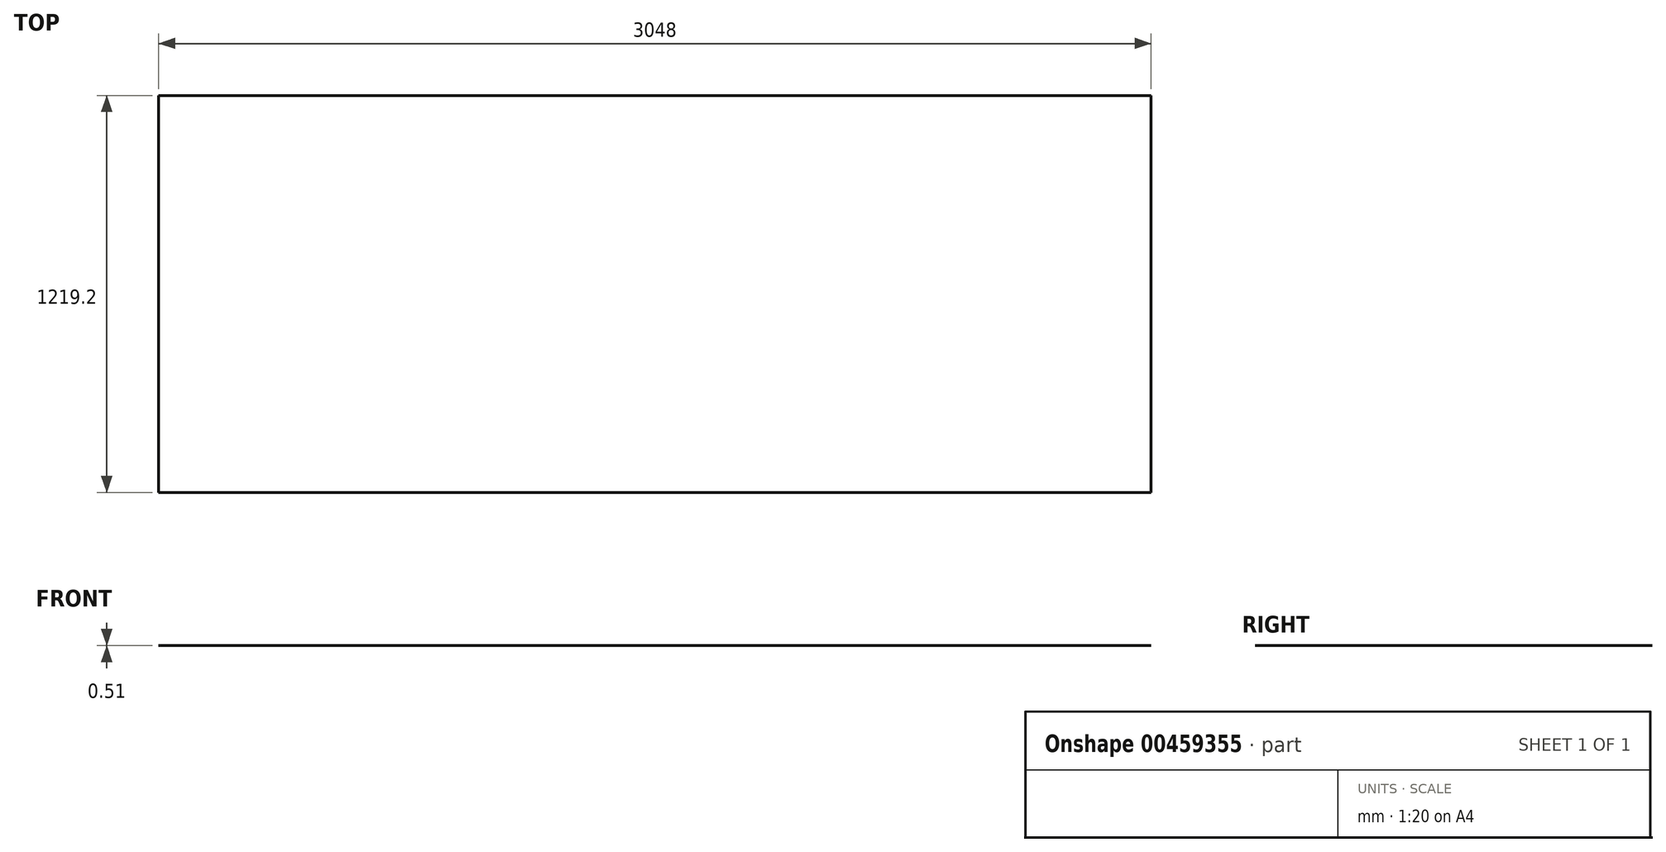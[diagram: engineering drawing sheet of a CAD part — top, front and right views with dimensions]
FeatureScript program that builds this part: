
annotation { "Feature Type Name" : "Feature", "Feature Type Description" : "" }
export const myFeature = defineFeature(function(context is Context, id is Id, definition is map)
    precondition{}
    {
        {
            var Q0;
            Q0=qCreatedBy(makeId("Top.planeOp"),FACE);
            var sketch = newSketch(context, id + "F0", { "sketchPlane" : qUnion([Q0])});
            skLineSegment(sketch, "E0.bottom", {"start": v(1524, 609.6) * mm, "end": v(-1524, 609.6) * mm});
            skLineSegment(sketch, "E0.top", {"start": v(1524, -609.6) * mm, "end": v(-1524, -609.6) * mm});
            skLineSegment(sketch, "E0.left", {"start": v(1524, 609.6) * mm, "end": v(1524, -609.6) * mm});
            skLineSegment(sketch, "E0.right", {"start": v(-1524, 609.6) * mm, "end": v(-1524, -609.6) * mm});
            skPoint(sketch, "E0.middle", {"position": v(0, 0) * mm});
            skSolve(sketch);
        }
        {
            var Q0;
            Q0=makeQuery(id+"F0.imprint","IMPRINT",FACE,{"disambiguationData":[TD([[makeQuery(id+"F0.imprint","IMPRINT",EDGE,{"derivedFrom":sQuery(id+"F0.wireOp",EDGE,"E0.bottom")}),1.0]])]});
            extrude(context, id + "F1", {"entities" : qUnion([Q0]), "depth" : 0.5 * mm});
        }
    });
